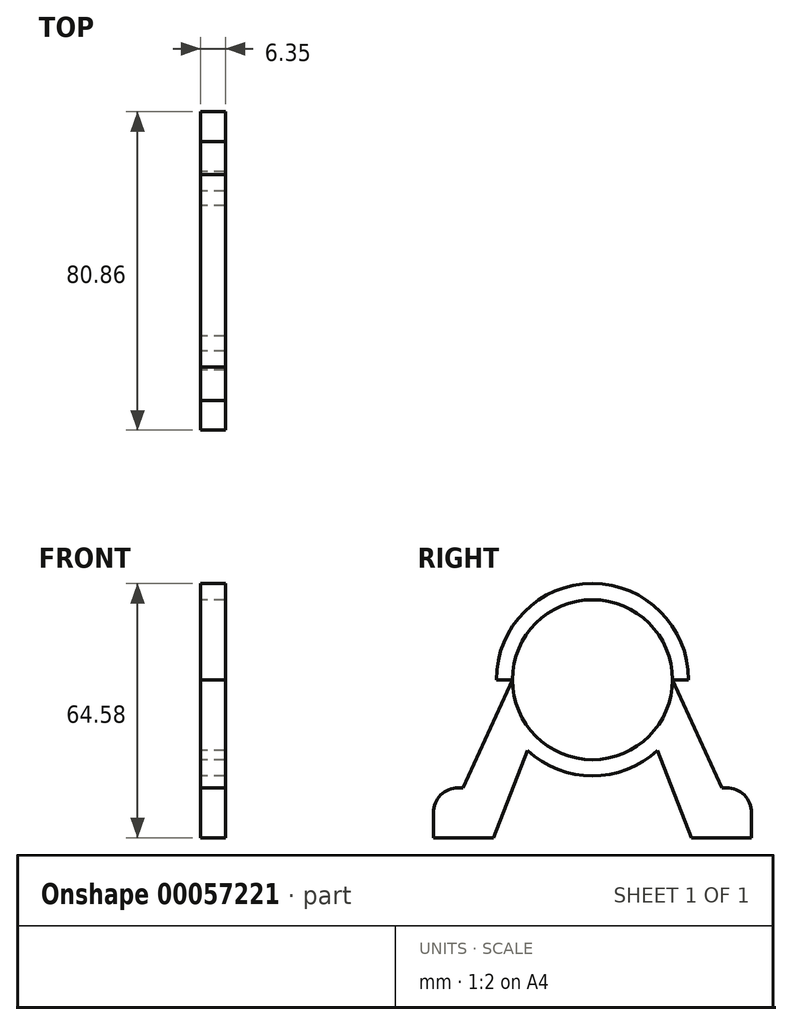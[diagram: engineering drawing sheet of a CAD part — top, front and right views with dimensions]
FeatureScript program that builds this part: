
annotation { "Feature Type Name" : "Feature", "Feature Type Description" : "" }
export const myFeature = defineFeature(function(context is Context, id is Id, definition is map)
    precondition{}
    {
        {
            var Q0;
            Q0=qCreatedBy(makeId("Right.planeOp"),FACE);
            var sketch = newSketch(context, id + "F0", { "sketchPlane" : qUnion([Q0])});
            skCircle(sketch, "E0", {"center": v(0, 0) * mm, "radius": 20.32 * mm});
            skLineSegment(sketch, "E1", {"start": v(-20.32, 0) * mm, "end": v(-38.67, -40.16) * mm});
            skLineSegment(sketch, "E2", {"start": v(-38.67, -40.16) * mm, "end": v(-25.19, -40.16) * mm});
            skLineSegment(sketch, "E3", {"start": v(-25.19, -40.16) * mm, "end": v(-14.94, -13.77) * mm});
            skLineSegment(sketch, "E4", {"start": v(-45.77, -40.16) * mm, "end": v(51.27, -40.16) * mm, "construction": true});
            skLineSegment(sketch, "E5.MirrorCS", {"start": v(20.32, 0) * mm, "end": v(38.67, -40.16) * mm});
            skLineSegment(sketch, "E6.MirrorCS", {"start": v(25.19, -40.16) * mm, "end": v(14.94, -13.77) * mm});
            skLineSegment(sketch, "E7.MirrorCS", {"start": v(38.67, -40.16) * mm, "end": v(25.19, -40.16) * mm});
            skCircle(sketch, "E8", {"center": v(0, 0) * mm, "radius": 24.42 * mm});
            skLineSegment(sketch, "E9", {"start": v(-24.42, 0) * mm, "end": v(24.42, 0) * mm});
            skLineSegment(sketch, "E10.bottom", {"start": v(-25.19, -40.16) * mm, "end": v(-40.43, -40.16) * mm});
            skLineSegment(sketch, "E10.top", {"start": v(-25.19, -27.46) * mm, "end": v(-34.08, -27.46) * mm});
            skLineSegment(sketch, "E10.left", {"start": v(-25.19, -40.16) * mm, "end": v(-25.19, -27.46) * mm});
            skLineSegment(sketch, "E10.right", {"start": v(-40.43, -40.16) * mm, "end": v(-40.43, -33.8) * mm});
            skLineSegment(sketch, "E11.bottom", {"start": v(25.19, -40.16) * mm, "end": v(40.43, -40.16) * mm});
            skLineSegment(sketch, "E11.top", {"start": v(25.19, -27.46) * mm, "end": v(34.08, -27.46) * mm});
            skLineSegment(sketch, "E11.left", {"start": v(25.19, -40.16) * mm, "end": v(25.19, -27.46) * mm});
            skLineSegment(sketch, "E11.right", {"start": v(40.43, -40.16) * mm, "end": v(40.43, -33.8) * mm});
            skPoint(sketch, "E12.visualSharp", {"position": v(-40.43, -27.46) * mm});
            skArc(sketch, "E12.filletArc", {"start": v(-34.08, -27.46) * mm, "mid": v(-38.57, -29.32) * mm, "end": v(-40.43, -33.8) * mm});
            skPoint(sketch, "E13.visualSharp", {"position": v(40.43, -27.46) * mm});
            skArc(sketch, "E13.filletArc", {"start": v(40.43, -33.8) * mm, "mid": v(38.57, -29.32) * mm, "end": v(34.08, -27.46) * mm});
            skSolve(sketch);
        }
        {
            var Q0;
            {var subQ0=sQuery(id+"F0.wireOp",EDGE,"E2");Q0=makeQuery(id+"F0.imprint","IMPRINT",FACE,{"disambiguationData":[TD([[makeQuery(id+"F0.imprint","IMPRINT",EDGE,{"derivedFrom":subQ0}),1.0]])]});}
            var Q1;
            {var subQ1=sQuery(id+"F0.wireOp",EDGE,"E0");var subQ3=sQuery(id+"F0.wireOp",EDGE,"E3");var subQ4=makeQuery(id+"F0.imprint","INTERSECT",VERTEX,{"derivedFrom":[subQ1,subQ3]});Q1=makeQuery(id+"F0.imprint","IMPRINT",FACE,{"disambiguationData":[TD([[makeQuery(id+"F0.imprint","IMPRINT",EDGE,{"disambiguationData":[TD([[subQ4,1.0]])],"derivedFrom":subQ3}),1.0]])]});}
            var Q2;
            {var subQ0=sQuery(id+"F0.wireOp",EDGE,"E3");var subQ1=sQuery(id+"F0.wireOp",EDGE,"E0");var subQ2=makeQuery(id+"F0.imprint","INTERSECT",VERTEX,{"derivedFrom":[subQ1,subQ0]});Q2=makeQuery(id+"F0.imprint","IMPRINT",FACE,{"disambiguationData":[TD([[makeQuery(id+"F0.imprint","IMPRINT",EDGE,{"disambiguationData":[TD([[subQ2,-1.0]])],"derivedFrom":subQ1}),-1.0]])]});}
            var Q3;
            {var subQ1=sQuery(id+"F0.wireOp",EDGE,"E0");var subQ3=sQuery(id+"F0.wireOp",EDGE,"E6.MirrorCS");var subQ4=makeQuery(id+"F0.imprint","INTERSECT",VERTEX,{"derivedFrom":[subQ1,subQ3]});Q3=makeQuery(id+"F0.imprint","IMPRINT",FACE,{"disambiguationData":[TD([[makeQuery(id+"F0.imprint","IMPRINT",EDGE,{"disambiguationData":[TD([[subQ4,1.0]])],"derivedFrom":subQ3}),-1.0]])]});}
            var Q4;
            {var subQ0=sQuery(id+"F0.wireOp",EDGE,"E7.MirrorCS");Q4=makeQuery(id+"F0.imprint","IMPRINT",FACE,{"disambiguationData":[TD([[makeQuery(id+"F0.imprint","IMPRINT",EDGE,{"derivedFrom":subQ0}),-1.0]])]});}
            var Q5;
            {var subQ0=sQuery(id+"F0.wireOp",EDGE,"E9");var subQ3=sQuery(id+"F0.wireOp",EDGE,"E8");var subQ5=makeQuery(id+"F0.imprint","INTERSECT",VERTEX,{"disambiguationData":[OD(1.0)],"derivedFrom":[subQ3,subQ0]});Q5=makeQuery(id+"F0.imprint","IMPRINT",FACE,{"disambiguationData":[TD([[makeQuery(id+"F0.imprint","IMPRINT",EDGE,{"disambiguationData":[TD([[subQ5,1.0]])],"derivedFrom":subQ3}),1.0]])]});}
            var Q6;
            {var subQ0=sQuery(id+"F0.wireOp",EDGE,"E9");var subQ3=sQuery(id+"F0.wireOp",EDGE,"E8");var subQ5=makeQuery(id+"F0.imprint","INTERSECT",VERTEX,{"disambiguationData":[OD(0.0)],"derivedFrom":[subQ3,subQ0]});Q6=makeQuery(id+"F0.imprint","IMPRINT",FACE,{"disambiguationData":[TD([[makeQuery(id+"F0.imprint","IMPRINT",EDGE,{"disambiguationData":[TD([[subQ5,-1.0]])],"derivedFrom":subQ3}),1.0]])]});}
            var Q7;
            {var subQ0=sQuery(id+"F0.wireOp",EDGE,"E10.left");Q7=makeQuery(id+"F0.imprint","IMPRINT",FACE,{"disambiguationData":[TD([[makeQuery(id+"F0.imprint","IMPRINT",EDGE,{"derivedFrom":subQ0}),-1.0]])]});}
            var Q8;
            {var subQ5=sQuery(id+"F0.wireOp",EDGE,"E10.left");Q8=makeQuery(id+"F0.imprint","IMPRINT",FACE,{"disambiguationData":[TD([[makeQuery(id+"F0.imprint","IMPRINT",EDGE,{"derivedFrom":subQ5}),1.0]])]});}
            var Q9;
            {var subQ5=sQuery(id+"F0.wireOp",EDGE,"E11.left");Q9=makeQuery(id+"F0.imprint","IMPRINT",FACE,{"disambiguationData":[TD([[makeQuery(id+"F0.imprint","IMPRINT",EDGE,{"derivedFrom":subQ5}),-1.0]])]});}
            var Q10;
            {var subQ0=sQuery(id+"F0.wireOp",EDGE,"E11.left");Q10=makeQuery(id+"F0.imprint","IMPRINT",FACE,{"disambiguationData":[TD([[makeQuery(id+"F0.imprint","IMPRINT",EDGE,{"derivedFrom":subQ0}),1.0]])]});}
            var Q11;
            {var subQ0=sQuery(id+"F0.wireOp",EDGE,"E11.right");Q11=makeQuery(id+"F0.imprint","IMPRINT",FACE,{"disambiguationData":[TD([[makeQuery(id+"F0.imprint","IMPRINT",EDGE,{"derivedFrom":subQ0}),1.0]])]});}
            var Q12;
            {var subQ0=sQuery(id+"F0.wireOp",EDGE,"E10.right");Q12=makeQuery(id+"F0.imprint","IMPRINT",FACE,{"disambiguationData":[TD([[makeQuery(id+"F0.imprint","IMPRINT",EDGE,{"derivedFrom":subQ0}),-1.0]])]});}
            extrude(context, id + "F1", {"entities" : qUnion([Q0, Q1, Q2, Q3, Q4, Q5, Q6, Q7, Q8, Q9, Q10, Q11, Q12]), "depth" : 6.35 * mm});
        }
    });
